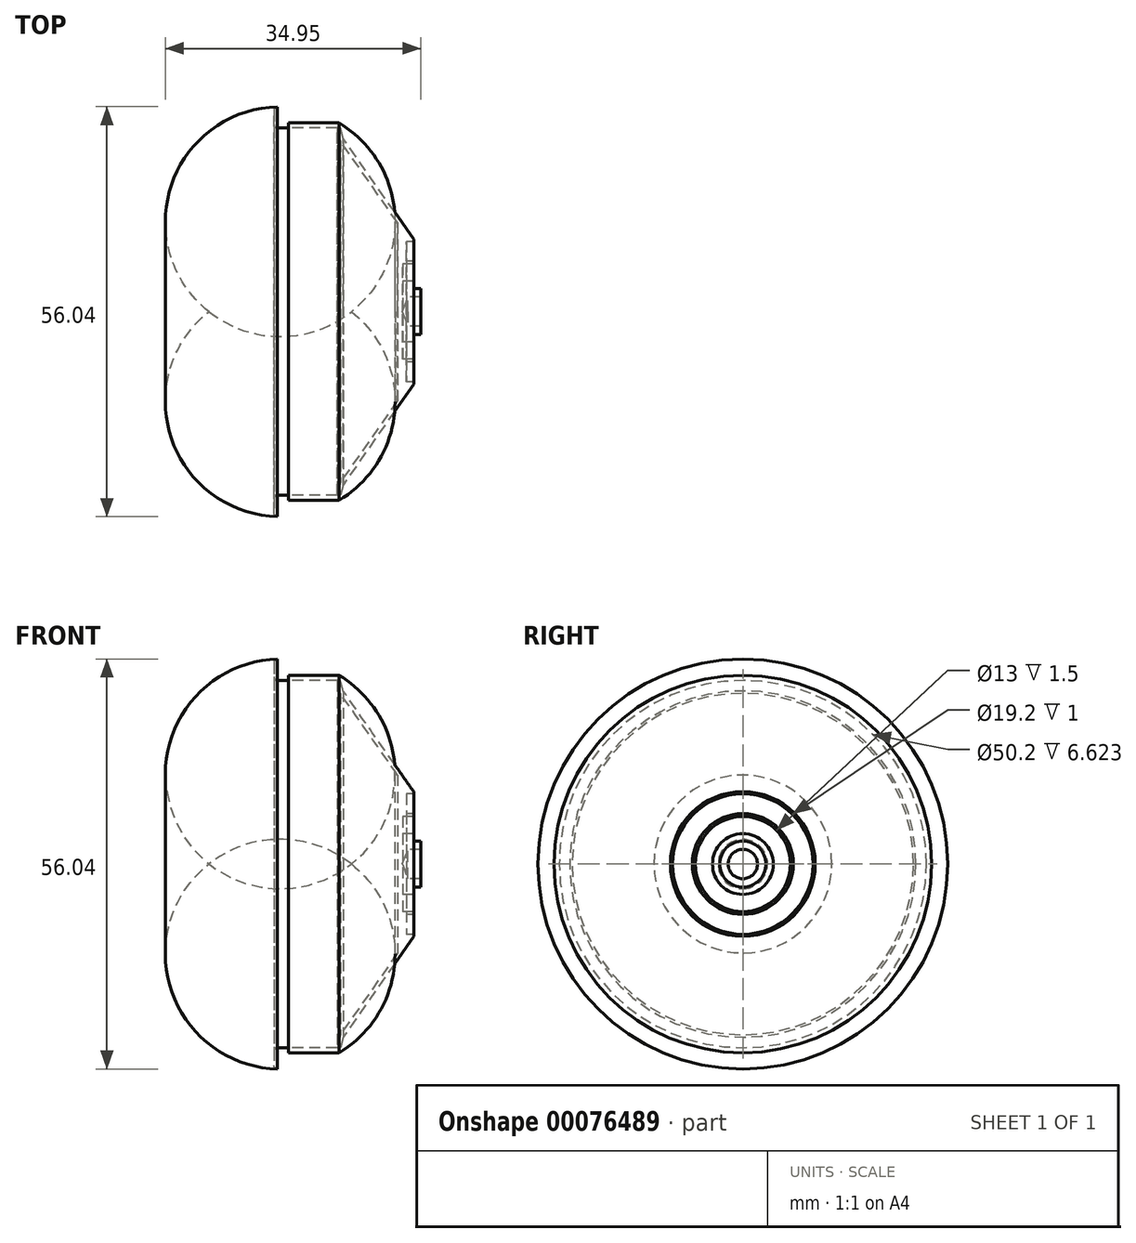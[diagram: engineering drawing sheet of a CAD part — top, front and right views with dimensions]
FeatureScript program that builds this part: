
annotation { "Feature Type Name" : "Feature", "Feature Type Description" : "" }
export const myFeature = defineFeature(function(context is Context, id is Id, definition is map)
    precondition{}
    {
        {
            var Q0;
            Q0=qCreatedBy(makeId("Front.planeOp"),FACE);
            var sketch = newSketch(context, id + "F0", { "sketchPlane" : qUnion([Q0])});
            skLineSegment(sketch, "E0", {"start": v(-1.4, 2) * mm, "end": v(-3.2, 2) * mm});
            skLineSegment(sketch, "E1", {"start": v(-3.2, 2) * mm, "end": v(-3.93, 0) * mm});
            skLineSegment(sketch, "E2", {"start": v(-4.6, 12.17) * mm, "end": v(-12.42, 23.34) * mm});
            skLineSegment(sketch, "E3", {"start": v(-1.4, 3.15) * mm, "end": v(-2.4, 3.15) * mm});
            skLineSegment(sketch, "E4", {"start": v(-2.4, 3.15) * mm, "end": v(-2.4, 4.15) * mm});
            skLineSegment(sketch, "E5", {"start": v(-2.4, 4.15) * mm, "end": v(-3.9, 4.15) * mm});
            skLineSegment(sketch, "E6", {"start": v(-3.9, 4.15) * mm, "end": v(-3.9, 6.5) * mm});
            skLineSegment(sketch, "E7", {"start": v(-3.9, 6.5) * mm, "end": v(-2.4, 6.5) * mm});
            skLineSegment(sketch, "E8", {"start": v(-2.4, 6.5) * mm, "end": v(-2.4, 6.9) * mm});
            skLineSegment(sketch, "E9", {"start": v(-2.4, 6.9) * mm, "end": v(-3.4, 6.9) * mm});
            skLineSegment(sketch, "E10", {"start": v(-3.4, 6.9) * mm, "end": v(-3.4, 9.6) * mm});
            skLineSegment(sketch, "E11", {"start": v(-3.4, 9.6) * mm, "end": v(-2.4, 9.6) * mm});
            skLineSegment(sketch, "E12", {"start": v(-2.4, 9.6) * mm, "end": v(-2.4, 9.9) * mm});
            skLineSegment(sketch, "E13", {"start": v(-1.4, 3.15) * mm, "end": v(-1.4, 2) * mm});
            skLineSegment(sketch, "E14", {"start": v(-12.04, 23.67) * mm, "end": v(-2.4, 9.9) * mm});
            skLineSegment(sketch, "E15", {"start": v(-4.6, 0) * mm, "end": v(-4.6, 12.17) * mm});
            skLineSegment(sketch, "E16", {"start": v(-21.5, 25.8) * mm, "end": v(-21.5, 25.1) * mm});
            skLineSegment(sketch, "E17", {"start": v(-4.6, 0) * mm, "end": v(-3.93, 0) * mm});
            skLineSegment(sketch, "E18", {"start": v(-19.5, 25.1) * mm, "end": v(-12.88, 25.1) * mm});
            skLineSegment(sketch, "E19", {"start": v(-19.5, 25.8) * mm, "end": v(-12.6, 25.8) * mm});
            skPoint(sketch, "E20.end.orphan", {"position": v(-21.5, 28) * mm});
            skLineSegment(sketch, "E21", {"start": v(-21.5, 28) * mm, "end": v(-14.97, 28) * mm});
            skLineSegment(sketch, "E22", {"start": v(-12.42, 23.34) * mm, "end": v(-12.88, 25.1) * mm});
            skLineSegment(sketch, "E23", {"start": v(-12.04, 23.67) * mm, "end": v(-12.6, 25.8) * mm});
            skLineSegment(sketch, "E24", {"start": v(-19.5, 25.8) * mm, "end": v(-19.5, 25.1) * mm});
            skSolve(sketch);
        }
        {
            var Q0;
            Q0=qSketchRegion(id+"F0",true);
            var Q1;
            Q1=sQuery(id+"F0.wireOp",EDGE,"E17");
            revolve(context, id + "F1", {"entities" : qUnion([Q0]), "axis" : qUnion([Q1]), "revolveType" : RevolveType.FULL});
        }
        {
            var Q0;
            Q0=qCreatedBy(makeId("Front.planeOp"),FACE);
            var sketch = newSketch(context, id + "F2", { "sketchPlane" : qUnion([Q0])});
            skLineSegment(sketch, "E25", {"start": v(-19.5, 25.8) * mm, "end": v(-12.6, 25.8) * mm});
            skPoint(sketch, "E26.orphan", {"position": v(-13.86, -26.32) * mm});
            skLineSegment(sketch, "E27", {"start": v(-21.5, 27.52) * mm, "end": v(-21.5, 25.6) * mm});
            skLineSegment(sketch, "E28", {"start": v(-24.7, 0) * mm, "end": v(0, 0) * mm});
            skArc(sketch, "E29", {"start": v(-12.6, 25.8) * mm, "mid": v(-16.65, 27.5) * mm, "end": v(-21.01, 28.02) * mm});
            skLineSegment(sketch, "E30", {"start": v(-21, 25.1) * mm, "end": v(-19.5, 25.1) * mm});
            skLineSegment(sketch, "E31", {"start": v(-19.5, 25.1) * mm, "end": v(-19.5, 25.8) * mm});
            skPoint(sketch, "E32.visualSharp", {"position": v(-21.5, 28) * mm});
            skArc(sketch, "E32.filletArc", {"start": v(-21.01, 28.02) * mm, "mid": v(-21.36, 27.87) * mm, "end": v(-21.5, 27.52) * mm});
            skPoint(sketch, "E33.visualSharp", {"position": v(-21.5, 25.1) * mm});
            skArc(sketch, "E33.filletArc", {"start": v(-21.5, 25.6) * mm, "mid": v(-21.35, 25.25) * mm, "end": v(-21, 25.1) * mm});
            skSolve(sketch);
        }
        {
            var Q0;
            Q0 = qSketchRegion(id + "F2", true);
            var Q1;
            Q1=sQuery(id+"F2.wireOp",EDGE,"E28");
            revolve(context, id + "F3", {"entities" : qUnion([Q0]), "axis" : qUnion([Q1]), "revolveType" : RevolveType.FULL});
        }
    });
